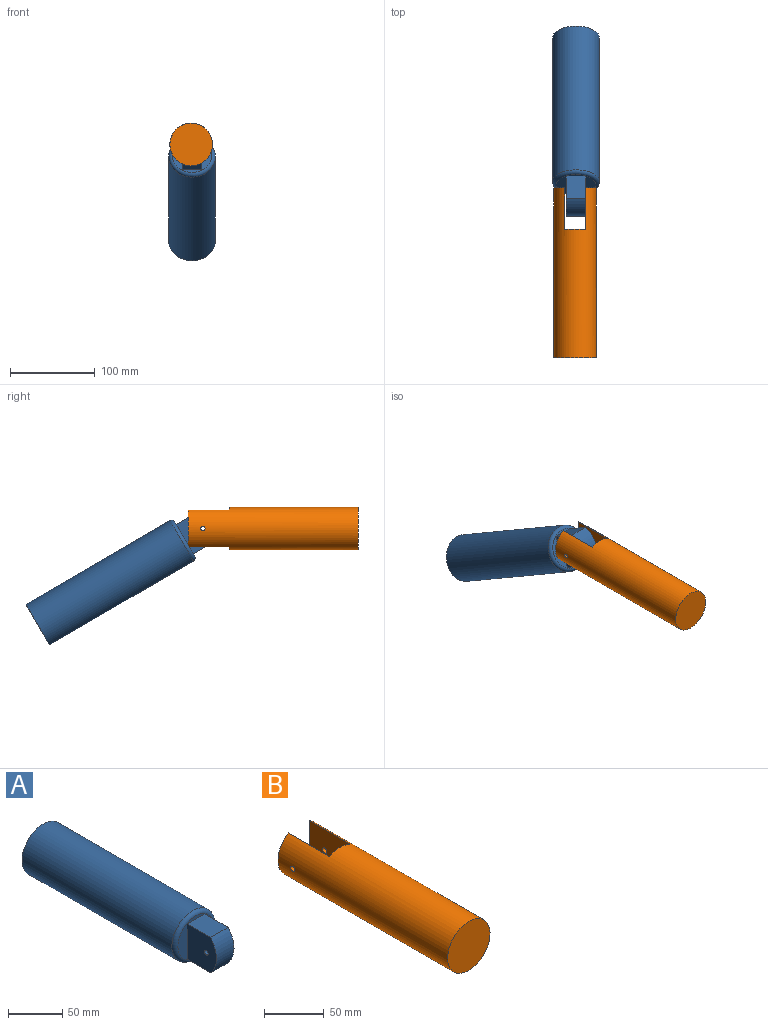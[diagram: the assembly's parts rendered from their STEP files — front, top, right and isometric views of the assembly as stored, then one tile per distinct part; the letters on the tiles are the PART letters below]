
ASSEMBLY  parts=2 mates=1
PART A: 10 faces, bbox 59.5x238.4x59.5 mm
  f0: plane 39.98x38.42mm, normal (-1,0,0), area 1420.4mm2, adj f2,f3,f4,f7,f8
  f1: plane 39.98x38.42mm, normal (1,0,0), area 1420.4mm2, adj f2,f3,f4,f7,f8
  f2: cylinder r=30mm len=39.98mm, axis (-1,0,0), area 1006.4mm2, adj f0,f1,f7,f8
  f3: cylinder r=2.5mm len=23mm, axis (-1,0,0), area 361.3mm2, adj f0,f1
  f4: plane 47x47mm, normal (0,-1,0), area 815.4mm2, adj f0,f1,f7,f8,f9
  f5: cylinder r=27.5mm len=196mm, axis (0,-1,0), area 33866.4mm2, adj f6,f9
  f6: plane 55x55mm, normal (0,1,0), area 2375.8mm2, adj f5
  f7: plane 30.78x23mm, normal (0,0,1), area 707.9mm2, adj f0,f1,f2,f4
  f8: plane 30.8x23mm, normal (0,0,-1), area 708.3mm2, adj f0,f1,f2,f4
  f9: torus R=23.5mm, axis (0,1,0), area 1028.3mm2, adj f4,f5
PART B: 9 faces, bbox 50x200x50 mm
  f0: cylinder r=25mm len=200mm, axis (0,-1,0), area 28841.5mm2, adj f1,f2,f3,f4,f5,f6,f7,f8
  f1: plane 43.3x12.5mm, normal (0,1,0), area 383.9mm2, adj f0,f5
  f2: plane 50x50mm, normal (0,-1,0), area 1963.5mm2, adj f0
  f3: plane 43.3x12.5mm, normal (0,1,0), area 383.9mm2, adj f0,f4
  f4: plane 48.42x43.3mm, normal (-1,0,0), area 2076.9mm2, adj f0,f3,f7,f8
  f5: plane 48.42x43.3mm, normal (1,0,0), area 2076.9mm2, adj f0,f1,f6,f8
  f6: cylinder r=2.5mm len=12.5mm, axis (1,0,0), area 195.4mm2, adj f0,f5
  f7: cylinder r=2.5mm len=12.5mm, axis (1,0,0), area 195.4mm2, adj f0,f4
  f8: plane 50x25mm, normal (0,1,0), area 1195.8mm2, adj f0,f4,f5
PLACE A rot(axis=(-1,0,0),30.2deg) t=(-39.26,83.53,7.66)mm
PLACE B t=(-40.26,-20.58,20.23)mm fixed
MATE revolute A.f3 <-> B.f6  axis (1,0,0) through (-27.76,61.92,20.23)mm
